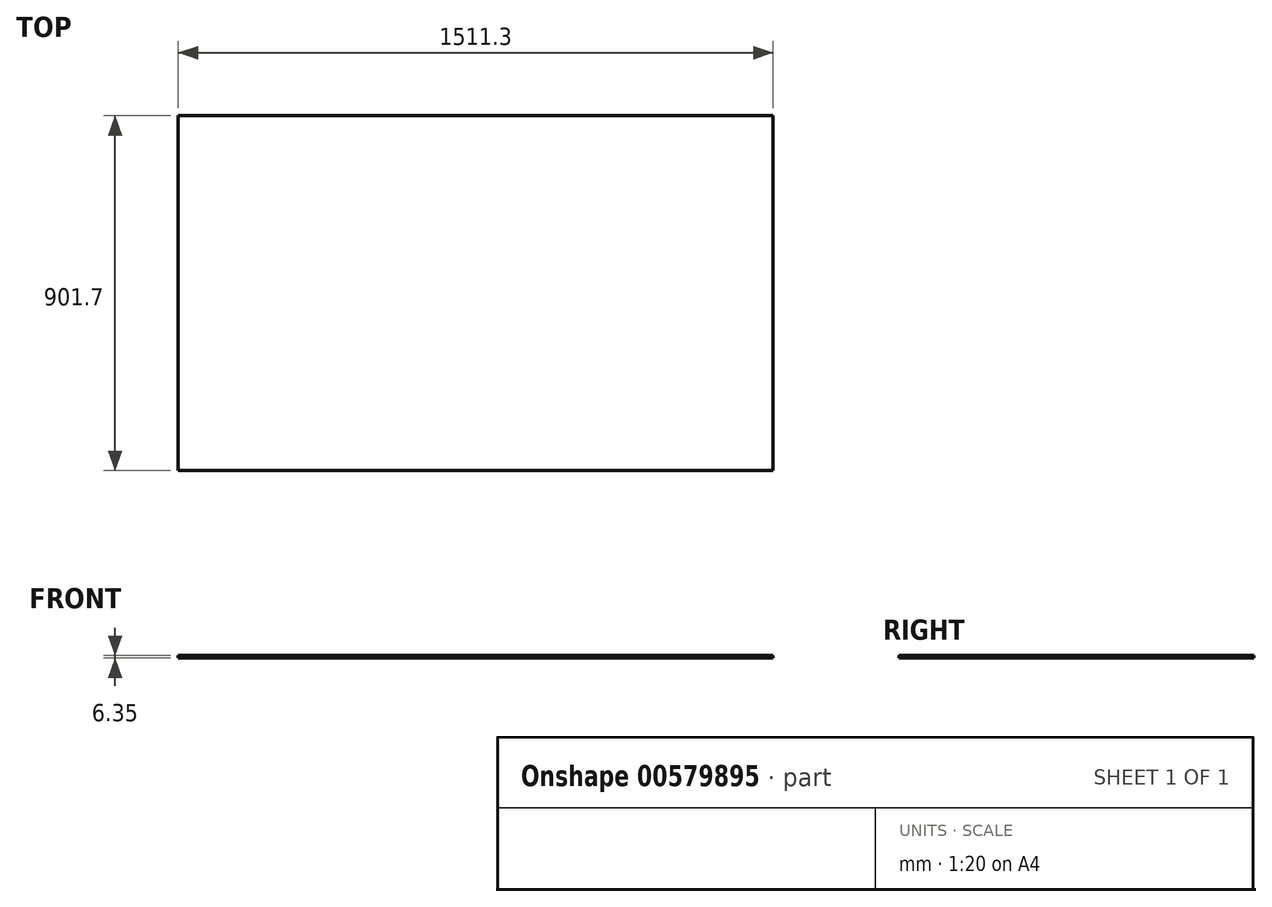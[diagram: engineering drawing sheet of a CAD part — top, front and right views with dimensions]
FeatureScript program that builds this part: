
annotation { "Feature Type Name" : "Feature", "Feature Type Description" : "" }
export const myFeature = defineFeature(function(context is Context, id is Id, definition is map)
    precondition{}
    {
        {
            var Q0;
            Q0=qCreatedBy(makeId("Top.planeOp"),FACE);
            var sketch = newSketch(context, id + "F0", { "sketchPlane" : qUnion([Q0])});
            skLineSegment(sketch, "E0", {"start": v(0, 0) * mm, "end": v(0, 901.7) * mm});
            skLineSegment(sketch, "E1", {"start": v(0, 901.7) * mm, "end": v(1511.3, 901.7) * mm});
            skLineSegment(sketch, "E2", {"start": v(1511.3, 901.7) * mm, "end": v(1511.3, 0) * mm});
            skLineSegment(sketch, "E3", {"start": v(1511.3, 0) * mm, "end": v(1066.8, 0) * mm});
            skLineSegment(sketch, "E4", {"start": v(444.5, 0) * mm, "end": v(0, 0) * mm});
            skLineSegment(sketch, "E5", {"start": v(444.5, 0) * mm, "end": v(1066.8, 0) * mm});
            skSolve(sketch);
        }
        {
            var Q0;
            Q0 = qSketchRegion(id + "F0", true);
            extrude(context, id + "F1", {"entities" : qUnion([Q0]), "depth" : 6.35 * mm, "offsetDistance" : 25.4 * mm});
        }
    });
